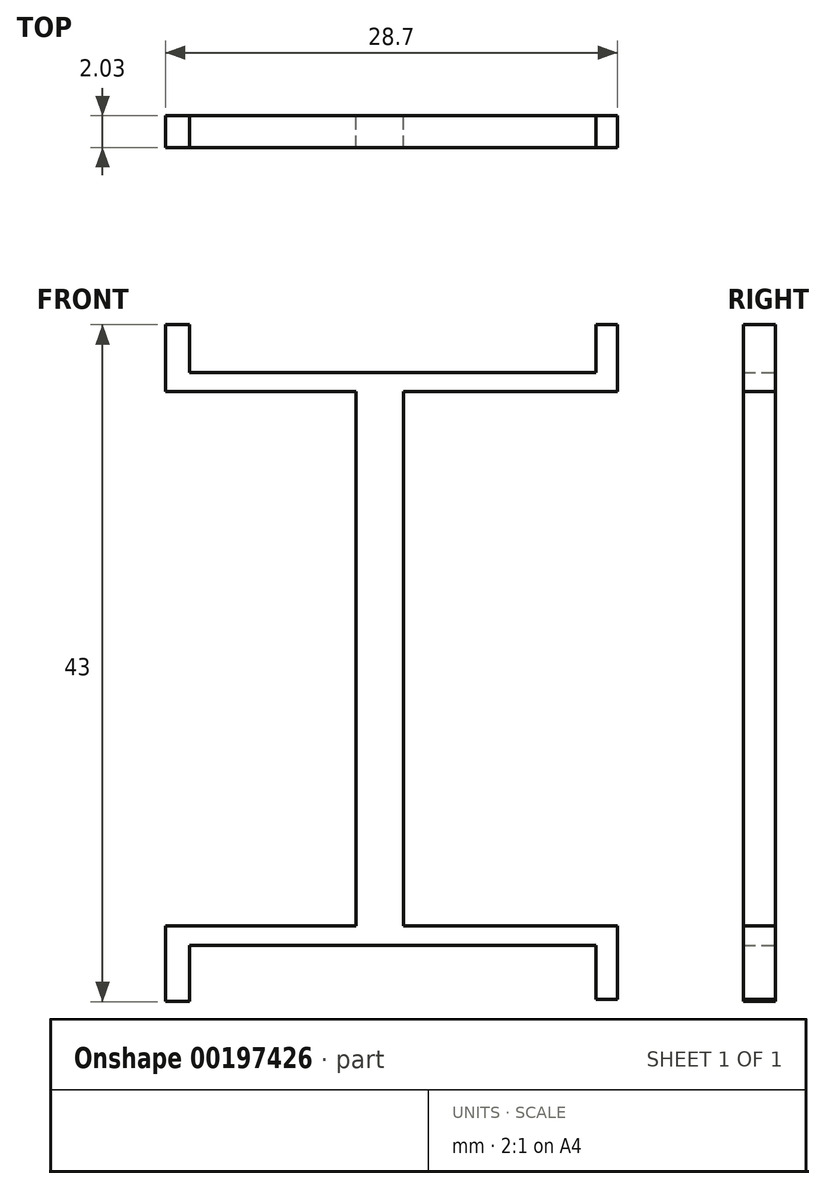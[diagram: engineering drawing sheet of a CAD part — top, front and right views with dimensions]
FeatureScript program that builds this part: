
annotation { "Feature Type Name" : "Feature", "Feature Type Description" : "" }
export const myFeature = defineFeature(function(context is Context, id is Id, definition is map)
    precondition{}
    {
        {
            var Q0;
            Q0=qCreatedBy(makeId("Front.planeOp"),FACE);
            var sketch = newSketch(context, id + "F0", { "sketchPlane" : qUnion([Q0])});
            skLineSegment(sketch, "E0.bottom", {"start": v(-33.93, 41.82) * mm, "end": v(-30.9, 41.82) * mm});
            skLineSegment(sketch, "E0.top", {"start": v(-33.93, 5.43) * mm, "end": v(-30.9, 5.43) * mm});
            skLineSegment(sketch, "E0.left", {"start": v(-33.93, 41.82) * mm, "end": v(-33.93, 5.43) * mm});
            skLineSegment(sketch, "E0.right", {"start": v(-30.9, 40.59) * mm, "end": v(-30.9, 5.43) * mm});
            skLineSegment(sketch, "E1.bottom", {"start": v(-30.9, 41.82) * mm, "end": v(-17.3, 41.82) * mm});
            skLineSegment(sketch, "E1.top", {"start": v(-30.9, 40.59) * mm, "end": v(-17.3, 40.59) * mm});
            skLineSegment(sketch, "E1.right", {"start": v(-17.3, 41.82) * mm, "end": v(-17.3, 40.59) * mm});
            skLineSegment(sketch, "E2.bottom", {"start": v(-33.93, 41.82) * mm, "end": v(-46.01, 41.82) * mm});
            skLineSegment(sketch, "E2.top", {"start": v(-33.93, 40.59) * mm, "end": v(-46.01, 40.59) * mm});
            skLineSegment(sketch, "E2.left", {"start": v(-33.93, 41.82) * mm, "end": v(-33.93, 40.59) * mm});
            skLineSegment(sketch, "E2.right", {"start": v(-46.01, 41.82) * mm, "end": v(-46.01, 40.59) * mm});
            skLineSegment(sketch, "E3.bottom", {"start": v(-33.93, 5.43) * mm, "end": v(-46.01, 5.43) * mm});
            skLineSegment(sketch, "E3.top", {"start": v(-33.93, 6.66) * mm, "end": v(-46.01, 6.66) * mm});
            skLineSegment(sketch, "E3.left", {"start": v(-33.93, 5.43) * mm, "end": v(-33.93, 6.66) * mm});
            skLineSegment(sketch, "E3.right", {"start": v(-46.01, 5.43) * mm, "end": v(-46.01, 6.66) * mm});
            skLineSegment(sketch, "E4.bottom", {"start": v(-30.9, 6.66) * mm, "end": v(-17.3, 6.66) * mm});
            skLineSegment(sketch, "E4.top", {"start": v(-30.9, 5.43) * mm, "end": v(-17.3, 5.43) * mm});
            skLineSegment(sketch, "E4.left", {"start": v(-30.9, 6.66) * mm, "end": v(-30.9, 5.43) * mm});
            skLineSegment(sketch, "E4.right", {"start": v(-17.3, 6.66) * mm, "end": v(-17.3, 5.43) * mm});
            skLineSegment(sketch, "E5.bottom", {"start": v(-46.01, 41.82) * mm, "end": v(-44.5, 41.82) * mm});
            skLineSegment(sketch, "E5.top", {"start": v(-46.01, 44.85) * mm, "end": v(-44.5, 44.85) * mm});
            skLineSegment(sketch, "E5.left", {"start": v(-46.01, 41.82) * mm, "end": v(-46.01, 44.85) * mm});
            skLineSegment(sketch, "E5.right", {"start": v(-44.5, 41.82) * mm, "end": v(-44.5, 44.85) * mm});
            skLineSegment(sketch, "E6.bottom", {"start": v(-17.3, 41.82) * mm, "end": v(-18.68, 41.82) * mm});
            skLineSegment(sketch, "E6.top", {"start": v(-17.3, 44.85) * mm, "end": v(-18.68, 44.85) * mm});
            skLineSegment(sketch, "E6.left", {"start": v(-17.3, 41.82) * mm, "end": v(-17.3, 44.85) * mm});
            skLineSegment(sketch, "E6.right", {"start": v(-18.68, 41.82) * mm, "end": v(-18.68, 44.85) * mm});
            skPoint(sketch, "E7.firstSnap0", {"position": v(-18.68, 43.34) * mm});
            skLineSegment(sketch, "E7.bottom", {"start": v(-18.68, 5.43) * mm, "end": v(-17.3, 5.43) * mm});
            skLineSegment(sketch, "E7.top", {"start": v(-18.68, 2) * mm, "end": v(-17.3, 2) * mm});
            skLineSegment(sketch, "E7.left", {"start": v(-18.68, 5.43) * mm, "end": v(-18.68, 2) * mm});
            skLineSegment(sketch, "E7.right", {"start": v(-17.3, 5.43) * mm, "end": v(-17.3, 2) * mm});
            skLineSegment(sketch, "E8.bottom", {"start": v(-46.01, 5.43) * mm, "end": v(-44.5, 5.43) * mm});
            skLineSegment(sketch, "E8.top", {"start": v(-46.01, 1.85) * mm, "end": v(-44.5, 1.85) * mm});
            skLineSegment(sketch, "E8.left", {"start": v(-46.01, 5.43) * mm, "end": v(-46.01, 1.85) * mm});
            skLineSegment(sketch, "E8.right", {"start": v(-44.5, 5.43) * mm, "end": v(-44.5, 1.85) * mm});
            skSolve(sketch);
        }
        {
            var Q0;
            Q0 = qSketchRegion(id + "F0", true);
            extrude(context, id + "F1", {"entities" : qUnion([Q0]), "depth" : 2.03 * mm});
        }
    });
